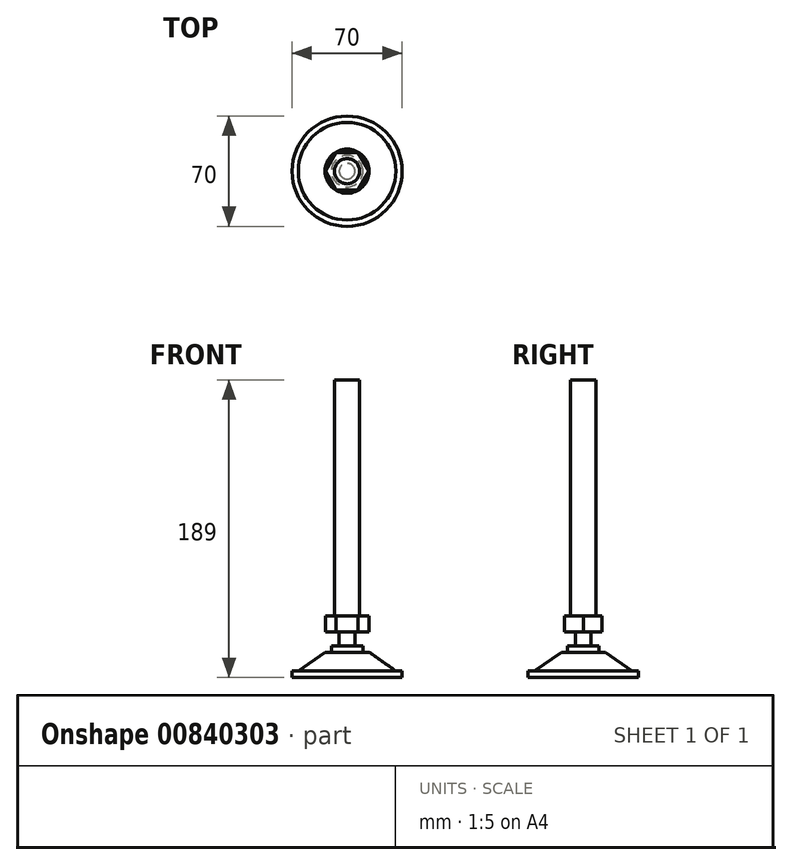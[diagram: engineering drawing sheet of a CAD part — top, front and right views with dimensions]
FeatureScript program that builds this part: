
annotation { "Feature Type Name" : "Feature", "Feature Type Description" : "" }
export const myFeature = defineFeature(function(context is Context, id is Id, definition is map)
    precondition{}
    {
        {
            var Q0;
            Q0=qCreatedBy(makeId("Right.planeOp"),FACE);
            var sketch = newSketch(context, id + "F0", { "sketchPlane" : qUnion([Q0])});
            skLineSegment(sketch, "E0", {"start": v(0, 0) * mm, "end": v(-35, 0) * mm});
            skLineSegment(sketch, "E1", {"start": v(-35, 0) * mm, "end": v(-35, 4) * mm});
            skLineSegment(sketch, "E2", {"start": v(-35, 4) * mm, "end": v(-31, 4) * mm});
            skLineSegment(sketch, "E3", {"start": v(-31, 4) * mm, "end": v(-14, 16) * mm});
            skLineSegment(sketch, "E4", {"start": v(-14, 16) * mm, "end": v(-10, 16) * mm});
            skLineSegment(sketch, "E5", {"start": v(-10, 16) * mm, "end": v(-10, 20) * mm});
            skLineSegment(sketch, "E6", {"start": v(-10, 20) * mm, "end": v(0, 20) * mm});
            skLineSegment(sketch, "E7", {"start": v(0, 20) * mm, "end": v(0, 0) * mm});
            skArc(sketch, "E8", {"start": v(-5, 20) * mm, "mid": v(-3.54, 16.46) * mm, "end": v(0, 15) * mm});
            skSolve(sketch);
        }
        {
            var Q0;
            {var subQ0=sQuery(id+"F0.wireOp",EDGE,"E0");Q0=makeQuery(id+"F0.imprint","IMPRINT",FACE,{"disambiguationData":[TD([[makeQuery(id+"F0.imprint","IMPRINT",EDGE,{"derivedFrom":subQ0}),-1.0]])]});}
            var Q1;
            Q1=sQuery(id+"F0.wireOp",EDGE,"E7");
            revolve(context, id + "F1", {"surfaceOperationType" : NewSurfaceOperationType.NEW, "entities" : qUnion([Q0]), "axis" : qUnion([Q1]), "revolveType" : RevolveType.FULL});
        }
        {
            var Q0;
            Q0=qCreatedBy(makeId("Right.planeOp"),FACE);
            var sketch = newSketch(context, id + "F2", { "sketchPlane" : qUnion([Q0])});
            skLineSegment(sketch, "E9", {"start": v(0, 39) * mm, "end": v(0, 189) * mm});
            skLineSegment(sketch, "E10", {"start": v(0, 189) * mm, "end": v(-8, 189) * mm});
            skLineSegment(sketch, "E11", {"start": v(-8, 189) * mm, "end": v(-8, 39) * mm});
            skLineSegment(sketch, "E12", {"start": v(-8, 39) * mm, "end": v(0, 39) * mm});
            skSolve(sketch);
        }
        {
            var Q0;
            Q0=makeQuery(id+"F2.imprint","IMPRINT",FACE,{"disambiguationData":[TD([[makeQuery(id+"F2.imprint","IMPRINT",EDGE,{"derivedFrom":sQuery(id+"F2.wireOp",EDGE,"E9")}),1.0]])]});
            var Q1;
            Q1=sQuery(id+"F2.wireOp",EDGE,"E9");
            revolve(context, id + "F3", {"surfaceOperationType" : NewSurfaceOperationType.NEW, "entities" : qUnion([Q0]), "axis" : qUnion([Q1]), "revolveType" : RevolveType.FULL});
        }
        {
            var Q0;
            Q0=makeQuery(id+"F3.opRevolve","SWEPT_FACE",FACE,{"disambiguationData":[OSD([sQuery(id+"F2.wireOp",EDGE,"E12")])]});
            var sketch = newSketch(context, id + "F4", { "sketchPlane" : qUnion([Q0])});
            skCircle(sketch, "E13.cCircle", {"center": v(0, 0) * mm, "radius": 12 * mm, "construction": true});
            skLineSegment(sketch, "E13.0", {"start": v(-6.93, 12) * mm, "end": v(6.93, 12) * mm});
            skLineSegment(sketch, "E13.1", {"start": v(6.93, 12) * mm, "end": v(13.86, 0) * mm});
            skLineSegment(sketch, "E13.2", {"start": v(13.86, 0) * mm, "end": v(6.93, -12) * mm});
            skLineSegment(sketch, "E13.3", {"start": v(6.93, -12) * mm, "end": v(-6.93, -12) * mm});
            skLineSegment(sketch, "E13.4", {"start": v(-6.93, -12) * mm, "end": v(-13.86, 0) * mm});
            skLineSegment(sketch, "E13.5", {"start": v(-13.86, 0) * mm, "end": v(-6.93, 12) * mm});
            skPoint(sketch, "E13.0.midPoint", {"position": v(0, 12) * mm});
            skSolve(sketch);
        }
        {
            var Q0;
            Q0 = qSketchRegion(id + "F4", true);
            extrude(context, id + "F5", {"entities" : qUnion([Q0]), "operationType" : NewBodyOperationType.ADD, "depth" : 10 * mm, "offsetDistance" : 25 * mm});
        }
        {
            var Q0;
            Q0=makeQuery(id+"F5.opExtrude","CAP_FACE",FACE,{"disambiguationData":[OSD([sQuery(id+"F4.wireOp",EDGE,"E13.0"),sQuery(id+"F4.wireOp",EDGE,"E13.1"),sQuery(id+"F4.wireOp",EDGE,"E13.2"),sQuery(id+"F4.wireOp",EDGE,"E13.3"),sQuery(id+"F4.wireOp",EDGE,"E13.4"),sQuery(id+"F4.wireOp",EDGE,"E13.5")])],"isStart":false});
            var sketch = newSketch(context, id + "F6", { "sketchPlane" : qUnion([Q0])});
            skCircle(sketch, "E14", {"center": v(0, 0) * mm, "radius": 5 * mm});
            skSolve(sketch);
        }
        {
            var Q0;
            Q0 = qSketchRegion(id + "F6", true);
            extrude(context, id + "F7", {"entities" : qUnion([Q0]), "operationType" : NewBodyOperationType.ADD, "endBound" : BoundingType.UP_TO_NEXT, "depth" : 25 * mm, "offsetDistance" : 25 * mm});
        }
    });
